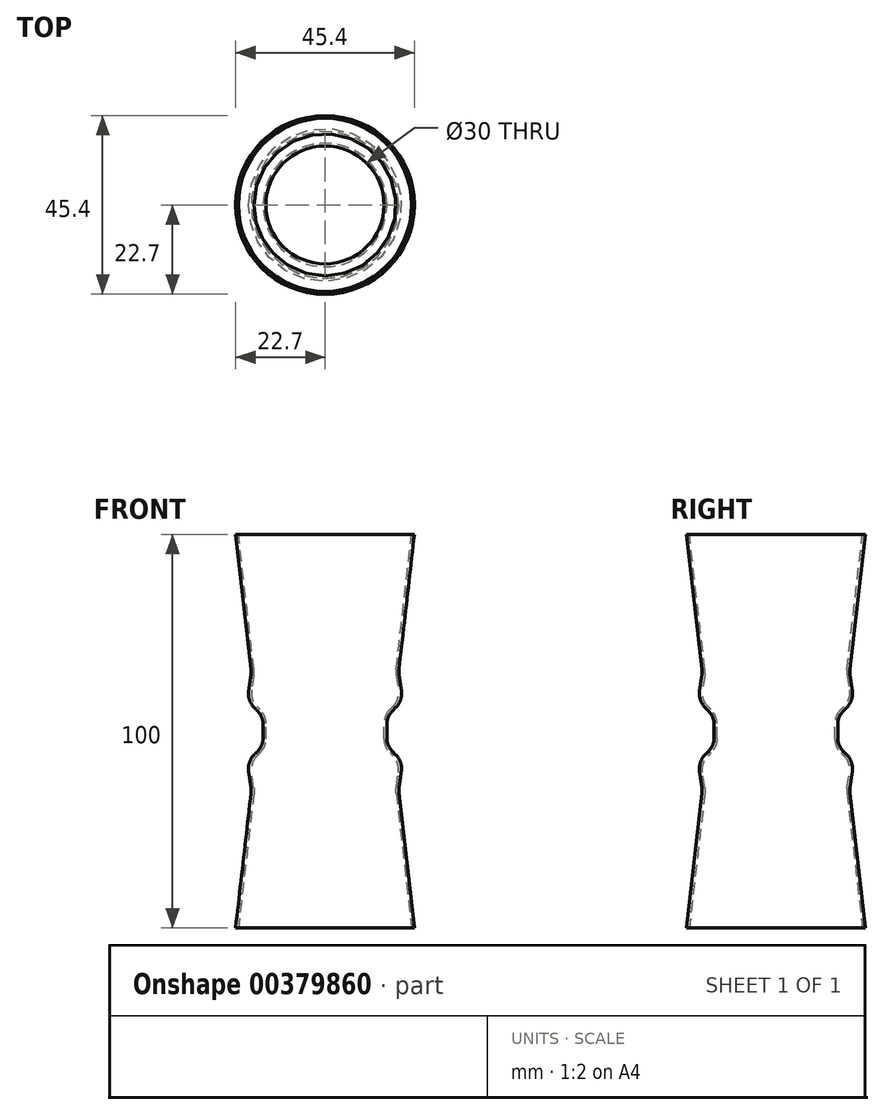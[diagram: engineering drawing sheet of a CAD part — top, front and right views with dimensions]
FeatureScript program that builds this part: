
annotation { "Feature Type Name" : "Feature", "Feature Type Description" : "" }
export const myFeature = defineFeature(function(context is Context, id is Id, definition is map)
    precondition{}
    {
        {
            var Q0;
            Q0=qCreatedBy(makeId("Front.planeOp"),FACE);
            var sketch = newSketch(context, id + "F0", { "sketchPlane" : qUnion([Q0])});
            skLineSegment(sketch, "E0", {"start": v(0, 0) * mm, "end": v(0, -50) * mm, "construction": true});
            skLineSegment(sketch, "E1", {"start": v(0, -50) * mm, "end": v(-22, -50) * mm, "construction": true});
            skLineSegment(sketch, "E2", {"start": v(-22, -50) * mm, "end": v(-18, -15) * mm});
            skLineSegment(sketch, "E3", {"start": v(-18, -15) * mm, "end": v(-19, -8) * mm});
            skLineSegment(sketch, "E4", {"start": v(-19, -8) * mm, "end": v(-15, -4) * mm});
            skLineSegment(sketch, "E5", {"start": v(-15, -4) * mm, "end": v(-15, 0) * mm});
            skLineSegment(sketch, "E6", {"start": v(-18, -15) * mm, "end": v(0, -15) * mm, "construction": true});
            skLineSegment(sketch, "E7", {"start": v(-19, -8) * mm, "end": v(0, -8) * mm, "construction": true});
            skLineSegment(sketch, "E8", {"start": v(-15, -4) * mm, "end": v(0, -4) * mm, "construction": true});
            skLineSegment(sketch, "E9", {"start": v(-15, 0) * mm, "end": v(0, 0) * mm, "construction": true});
            skLineSegment(sketch, "E10.0", {"start": v(-15.7, -3.71) * mm, "end": v(-15.7, 0) * mm});
            skLineSegment(sketch, "E10.1", {"start": v(-19.74, -7.75) * mm, "end": v(-15.7, -3.71) * mm});
            skLineSegment(sketch, "E10.2", {"start": v(-18.7, -15) * mm, "end": v(-19.74, -7.75) * mm});
            skLineSegment(sketch, "E10.3", {"start": v(-22.7, -50) * mm, "end": v(-18.7, -15) * mm});
            skLineSegment(sketch, "E11", {"start": v(-22.7, -50) * mm, "end": v(-22, -50) * mm});
            skLineSegment(sketch, "E12", {"start": v(-15.7, 0) * mm, "end": v(-15, 0) * mm});
            skLineSegment(sketch, "E13.MirrorCS", {"start": v(-22.7, 50) * mm, "end": v(-22, 50) * mm});
            skLineSegment(sketch, "E14.MirrorCS", {"start": v(-19, 8) * mm, "end": v(-15, 4) * mm});
            skLineSegment(sketch, "E15.MirrorCS", {"start": v(-15, 4) * mm, "end": v(-15, 0) * mm});
            skLineSegment(sketch, "E16.MirrorCS", {"start": v(-18.7, 15) * mm, "end": v(-19.74, 7.75) * mm});
            skLineSegment(sketch, "E17.MirrorCS", {"start": v(-18, 15) * mm, "end": v(-19, 8) * mm});
            skLineSegment(sketch, "E18.MirrorCS", {"start": v(-22, 50) * mm, "end": v(-18, 15) * mm});
            skLineSegment(sketch, "E19.MirrorCS", {"start": v(-15.7, 3.71) * mm, "end": v(-15.7, 0) * mm});
            skLineSegment(sketch, "E20.MirrorCS", {"start": v(-19.74, 7.75) * mm, "end": v(-15.7, 3.71) * mm});
            skLineSegment(sketch, "E21.MirrorCS", {"start": v(-22.7, 50) * mm, "end": v(-18.7, 15) * mm});
            skSolve(sketch);
        }
        {
            var Q0;
            Q0=makeQuery(id+"F0.imprint","IMPRINT",FACE,{"disambiguationData":[TD([[makeQuery(id+"F0.imprint","IMPRINT",EDGE,{"derivedFrom":sQuery(id+"F0.wireOp",EDGE,"E2")}),1.0]])]});
            var Q1;
            Q1=makeQuery(id+"F0.imprint","IMPRINT",FACE,{"disambiguationData":[TD([[makeQuery(id+"F0.imprint","IMPRINT",EDGE,{"derivedFrom":sQuery(id+"F0.wireOp",EDGE,"E12")}),1.0]])]});
            var Q2;
            Q2=sQuery(id+"F0.wireOp",EDGE,"E0");
            revolve(context, id + "F1", {"entities" : qUnion([Q0, Q1]), "axis" : qUnion([Q2]), "revolveType" : RevolveType.FULL});
        }
        {
            var Q0;
            Q0=makeQuery(id+"F1.opRevolve","SWEPT_EDGE",EDGE,{"disambiguationData":[OSD([sQuery(id+"F0.wireOp",EDGE,"E16.MirrorCS"),sQuery(id+"F0.wireOp",EDGE,"E20.MirrorCS")])]});
            var Q1;
            Q1=makeQuery(id+"F1.opRevolve","SWEPT_EDGE",EDGE,{"disambiguationData":[OSD([sQuery(id+"F0.wireOp",EDGE,"E14.MirrorCS"),sQuery(id+"F0.wireOp",EDGE,"E17.MirrorCS")])]});
            var Q2;
            Q2=makeQuery(id+"F1.opRevolve","SWEPT_EDGE",EDGE,{"disambiguationData":[OSD([sQuery(id+"F0.wireOp",EDGE,"E17.MirrorCS"),sQuery(id+"F0.wireOp",EDGE,"E18.MirrorCS")])]});
            var Q3;
            Q3=makeQuery(id+"F1.opRevolve","SWEPT_EDGE",EDGE,{"disambiguationData":[OSD([sQuery(id+"F0.wireOp",EDGE,"E16.MirrorCS"),sQuery(id+"F0.wireOp",EDGE,"E21.MirrorCS")])]});
            var Q4;
            Q4=makeQuery(id+"F1.opRevolve","SWEPT_EDGE",EDGE,{"disambiguationData":[OSD([sQuery(id+"F0.wireOp",EDGE,"E10.0"),sQuery(id+"F0.wireOp",EDGE,"E10.1")])]});
            var Q5;
            Q5=makeQuery(id+"F1.opRevolve","SWEPT_EDGE",EDGE,{"disambiguationData":[OSD([sQuery(id+"F0.wireOp",EDGE,"E10.1"),sQuery(id+"F0.wireOp",EDGE,"E10.2")])]});
            var Q6;
            Q6=makeQuery(id+"F1.opRevolve","SWEPT_EDGE",EDGE,{"disambiguationData":[OSD([sQuery(id+"F0.wireOp",EDGE,"E10.2"),sQuery(id+"F0.wireOp",EDGE,"E10.3")])]});
            var Q7;
            Q7=makeQuery(id+"F1.opRevolve","SWEPT_EDGE",EDGE,{"disambiguationData":[OSD([sQuery(id+"F0.wireOp",EDGE,"E2"),sQuery(id+"F0.wireOp",EDGE,"E3")])]});
            var Q8;
            Q8=makeQuery(id+"F1.opRevolve","SWEPT_EDGE",EDGE,{"disambiguationData":[OSD([sQuery(id+"F0.wireOp",EDGE,"E3"),sQuery(id+"F0.wireOp",EDGE,"E4")])]});
            var Q9;
            Q9=makeQuery(id+"F1.opRevolve","SWEPT_EDGE",EDGE,{"disambiguationData":[OSD([sQuery(id+"F0.wireOp",EDGE,"E4"),sQuery(id+"F0.wireOp",EDGE,"E5")])]});
            var Q10;
            Q10=makeQuery(id+"F1.opRevolve","SWEPT_EDGE",EDGE,{"disambiguationData":[OSD([sQuery(id+"F0.wireOp",EDGE,"E19.MirrorCS"),sQuery(id+"F0.wireOp",EDGE,"E20.MirrorCS")])]});
            var Q11;
            Q11=makeQuery(id+"F1.opRevolve","SWEPT_FACE",FACE,{"disambiguationData":[OSD([sQuery(id+"F0.wireOp",EDGE,"E5"),sQuery(id+"F0.wireOp",EDGE,"E15.MirrorCS")])]});
            fillet(context, id + "F2", {"entities" : qUnion([Q0, Q1, Q2, Q3, Q4, Q5, Q6, Q7, Q8, Q9, Q10, Q11]), "radius" : 5 * mm, "tangentPropagation" : true, "allowEdgeOverflow" : false});
        }
    });
